FCSTD DOCUMENT  (FreeCAD 0.15R4671 (Git))
Label: CheekyElevations
License: All rights reserved
LicenseURL: http://en.wikipedia.org/wiki/All_rights_reserved
objects: Sketcher::SketchObject×1
note: 1 computed .brp shape members not serialized (recipe doc carries the construction recipe); baked Part::Feature solids carry a one-line shape summary decoded from their .brp

FEATURE [Sketcher::SketchObject] Sketch
  sketch-geometry (10):
    g0: LineSegment StartX=0 StartY=0 StartZ=0 EndX=0 EndY=111.125 EndZ=0
    g1: LineSegment StartX=0 StartY=111.125 StartZ=0 EndX=9.525 EndY=111.125 EndZ=0
    g2: LineSegment StartX=0 StartY=0 StartZ=0 EndX=190.374 EndY=0 EndZ=0
    g3: LineSegment StartX=190.374 StartY=0 StartZ=0 EndX=190.374 EndY=55.3734 EndZ=0
    g4: ArcOfCircle CenterX=208.674 CenterY=435.934 CenterZ=0 NormalX=0 NormalY=0 NormalZ=1 Radius=381 StartAngle=4.16237 EndAngle=4.66434
    g5: LineSegment StartX=6.35 StartY=3.175 StartZ=0 EndX=6.35 EndY=104.775 EndZ=0
    g6: LineSegment StartX=6.35 StartY=104.775 StartZ=0 EndX=93.0211 EndY=64.3596 EndZ=0
    g7: LineSegment StartX=93.0211 StartY=64.3596 StartZ=0 EndX=187.199 EndY=47.7534 EndZ=0
    g8: LineSegment StartX=187.199 StartY=47.7534 StartZ=0 EndX=187.199 EndY=3.175 EndZ=0
    g9: LineSegment StartX=6.35 StartY=3.175 StartZ=0 EndX=187.199 EndY=3.175 EndZ=0
  constraints (30):
    c: Coincident(g0,g-1)
    c: PointOnObject(g0,g-2)
    c: Coincident(g1,g0)
    c: Horizontal(g1)
    c: Coincident(g2,g-1)
    c: Horizontal(g2)
    c: Coincident(g3,g2)
    c: Vertical(g3)
    c: Coincident(g4,g3)
    c: Coincident(g4,g1)
    c: DistanceX(g1) = 9.525
    c: Coincident(g7,g6)
    c: Coincident(g8,g7)
    c: Coincident(g9,g8)
    c: Horizontal(g9)
    c: DistanceY(g-1,g5) = 3.175
    c: DistanceX(g-1,g5) = 6.35
    c: DistanceX(g8,g2) = 3.175
    c: Distance(g6,g7) = 95.631
    c: Distance(g6,g5) = 95.631
    c: Angle(g7,g8) = 1.74533
    c: Angle(g7,g6) = 2.87979
    c: DistanceY(g3,g7) = -7.62
    c: DistanceY(g5,g5) = -101.6
    c: DistanceY(g0,g6) = -6.35
    c: Coincident(g6,g5)
    c: Vertical(g5)
    c: Coincident(g9,g5)
    c: Vertical(g8)
    c: Radius(g4) = 381
